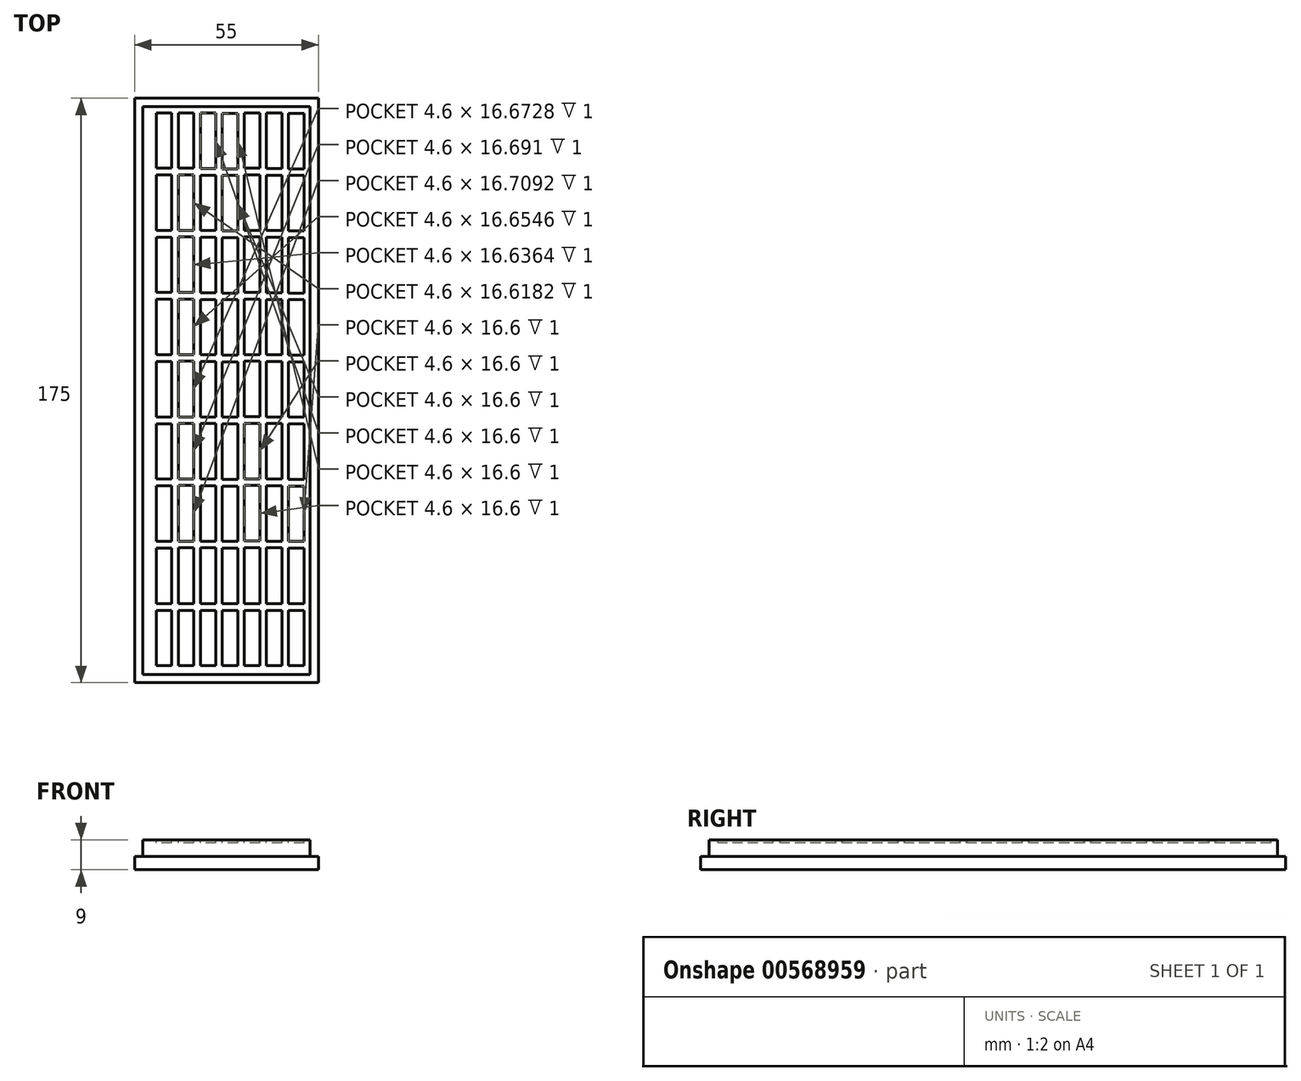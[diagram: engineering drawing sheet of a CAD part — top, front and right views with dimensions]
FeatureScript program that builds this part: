
annotation { "Feature Type Name" : "Feature", "Feature Type Description" : "" }
export const myFeature = defineFeature(function(context is Context, id is Id, definition is map)
    precondition{}
    {
        {
            var Q0;
            Q0=qCreatedBy(makeId("Top.planeOp"),FACE);
            var sketch = newSketch(context, id + "F0", { "sketchPlane" : qUnion([Q0])});
            skLineSegment(sketch, "E0.bottom", {"start": v(-26.96, 161.38) * mm, "end": v(28.04, 161.38) * mm});
            skLineSegment(sketch, "E0.top", {"start": v(-26.96, -13.62) * mm, "end": v(28.04, -13.62) * mm});
            skLineSegment(sketch, "E0.left", {"start": v(-26.96, 161.38) * mm, "end": v(-26.96, -13.62) * mm});
            skLineSegment(sketch, "E0.right", {"start": v(28.04, 161.38) * mm, "end": v(28.04, -13.62) * mm});
            skSolve(sketch);
        }
        {
            var Q0;
            Q0=makeQuery(id+"F0.imprint","IMPRINT",FACE,{"disambiguationData":[TD([[makeQuery(id+"F0.imprint","IMPRINT",EDGE,{"derivedFrom":sQuery(id+"F0.wireOp",EDGE,"E0.bottom")}),-1.0]])]});
            extrude(context, id + "F1", {"entities" : qUnion([Q0]), "depth" : 4 * mm, "offsetDistance" : 25.4 * mm});
        }
        {
            var Q0;
            Q0=makeQuery(id+"F1.opExtrude","CAP_FACE",FACE,{"disambiguationData":[OSD([sQuery(id+"F0.wireOp",EDGE,"E0.bottom"),sQuery(id+"F0.wireOp",EDGE,"E0.top"),sQuery(id+"F0.wireOp",EDGE,"E0.left"),sQuery(id+"F0.wireOp",EDGE,"E0.right")])],"isStart":false});
            var sketch = newSketch(context, id + "F2", { "sketchPlane" : qUnion([Q0])});
            skLineSegment(sketch, "E1.bottom", {"start": v(25.54, 158.88) * mm, "end": v(-24.46, 158.88) * mm});
            skLineSegment(sketch, "E1.top", {"start": v(25.54, -11.12) * mm, "end": v(-24.46, -11.12) * mm});
            skLineSegment(sketch, "E1.left", {"start": v(25.54, 158.88) * mm, "end": v(25.54, -11.12) * mm});
            skLineSegment(sketch, "E1.right", {"start": v(-24.46, 158.88) * mm, "end": v(-24.46, -11.12) * mm});
            skSolve(sketch);
        }
        {
            var Q0;
            Q0=makeQuery(id+"F2.imprint","IMPRINT",FACE,{"disambiguationData":[TD([[makeQuery(id+"F2.imprint","IMPRINT",EDGE,{"derivedFrom":sQuery(id+"F2.wireOp",EDGE,"E1.bottom")}),1.0]])]});
            extrude(context, id + "F3", {"entities" : qUnion([Q0]), "operationType" : NewBodyOperationType.ADD, "depth" : 5 * mm, "offsetDistance" : 25.4 * mm});
        }
        {
            var Q0;
            Q0=makeQuery(id+"F3.opExtrude","CAP_FACE",FACE,{"disambiguationData":[OSD([sQuery(id+"F2.wireOp",EDGE,"E1.bottom"),sQuery(id+"F2.wireOp",EDGE,"E1.top"),sQuery(id+"F2.wireOp",EDGE,"E1.left"),sQuery(id+"F2.wireOp",EDGE,"E1.right")])],"isStart":false});
            var sketch = newSketch(context, id + "F4", { "sketchPlane" : qUnion([Q0])});
            skLineSegment(sketch, "E2.bottom", {"start": v(23.73, 156.88) * mm, "end": v(19.13, 156.88) * mm});
            skLineSegment(sketch, "E2.top", {"start": v(23.73, 140.28) * mm, "end": v(19.13, 140.28) * mm});
            skLineSegment(sketch, "E2.left", {"start": v(23.73, 156.88) * mm, "end": v(23.73, 140.28) * mm});
            skLineSegment(sketch, "E2.right", {"start": v(19.13, 156.88) * mm, "end": v(19.13, 140.28) * mm});
            skLineSegment(sketch, "E3.bottom", {"start": v(23.73, 138.28) * mm, "end": v(19.13, 138.28) * mm});
            skLineSegment(sketch, "E3.top", {"start": v(23.73, 121.68) * mm, "end": v(19.13, 121.68) * mm});
            skLineSegment(sketch, "E3.left", {"start": v(23.73, 138.28) * mm, "end": v(23.73, 121.68) * mm});
            skLineSegment(sketch, "E3.right", {"start": v(19.13, 138.28) * mm, "end": v(19.13, 121.68) * mm});
            skLineSegment(sketch, "E4.1.0.0", {"start": v(17.13, 156.97) * mm, "end": v(12.53, 156.97) * mm});
            skLineSegment(sketch, "E4.1.0.1", {"start": v(17.13, 156.97) * mm, "end": v(17.13, 140.37) * mm});
            skLineSegment(sketch, "E4.1.0.2", {"start": v(12.53, 156.97) * mm, "end": v(12.53, 140.37) * mm});
            skLineSegment(sketch, "E4.1.0.3", {"start": v(17.13, 140.37) * mm, "end": v(12.53, 140.37) * mm});
            skLineSegment(sketch, "E4.1.0.4", {"start": v(17.13, 138.37) * mm, "end": v(12.53, 138.37) * mm});
            skLineSegment(sketch, "E4.1.0.5", {"start": v(17.13, 138.37) * mm, "end": v(17.13, 121.77) * mm});
            skLineSegment(sketch, "E4.1.0.6", {"start": v(12.53, 138.37) * mm, "end": v(12.53, 121.77) * mm});
            skLineSegment(sketch, "E4.1.0.7", {"start": v(17.13, 121.77) * mm, "end": v(12.53, 121.77) * mm});
            skLineSegment(sketch, "E4.2.0.0", {"start": v(10.53, 157.05) * mm, "end": v(5.93, 157.05) * mm});
            skLineSegment(sketch, "E4.2.0.1", {"start": v(10.53, 157.05) * mm, "end": v(10.53, 140.45) * mm});
            skLineSegment(sketch, "E4.2.0.2", {"start": v(5.93, 157.05) * mm, "end": v(5.93, 140.45) * mm});
            skLineSegment(sketch, "E4.2.0.3", {"start": v(10.53, 140.45) * mm, "end": v(5.93, 140.45) * mm});
            skLineSegment(sketch, "E4.2.0.4", {"start": v(10.53, 138.45) * mm, "end": v(5.93, 138.45) * mm});
            skLineSegment(sketch, "E4.2.0.5", {"start": v(10.53, 138.45) * mm, "end": v(10.53, 121.85) * mm});
            skLineSegment(sketch, "E4.2.0.6", {"start": v(5.93, 138.45) * mm, "end": v(5.93, 121.85) * mm});
            skLineSegment(sketch, "E4.2.0.7", {"start": v(10.53, 121.85) * mm, "end": v(5.93, 121.85) * mm});
            skLineSegment(sketch, "E5.0.1.0", {"start": v(23.73, 119.68) * mm, "end": v(19.13, 119.68) * mm});
            skLineSegment(sketch, "E5.0.1.1", {"start": v(23.73, 119.68) * mm, "end": v(23.73, 103.08) * mm});
            skLineSegment(sketch, "E5.0.1.2", {"start": v(19.13, 119.68) * mm, "end": v(19.13, 103.08) * mm});
            skLineSegment(sketch, "E5.0.1.3", {"start": v(17.13, 119.77) * mm, "end": v(17.13, 103.17) * mm});
            skLineSegment(sketch, "E5.0.1.4", {"start": v(23.73, 103.08) * mm, "end": v(19.13, 103.08) * mm});
            skLineSegment(sketch, "E5.0.1.5", {"start": v(23.73, 101.08) * mm, "end": v(19.13, 101.08) * mm});
            skLineSegment(sketch, "E5.0.1.6", {"start": v(23.73, 101.08) * mm, "end": v(23.73, 84.48) * mm});
            skLineSegment(sketch, "E5.0.1.7", {"start": v(23.73, 84.48) * mm, "end": v(19.13, 84.48) * mm});
            skLineSegment(sketch, "E5.0.1.8", {"start": v(17.13, 101.17) * mm, "end": v(17.13, 84.57) * mm});
            skLineSegment(sketch, "E5.0.1.9", {"start": v(19.13, 101.08) * mm, "end": v(19.13, 84.48) * mm});
            skLineSegment(sketch, "E5.0.1.10", {"start": v(17.13, 101.17) * mm, "end": v(12.53, 101.17) * mm});
            skLineSegment(sketch, "E5.0.1.11", {"start": v(17.13, 103.17) * mm, "end": v(12.53, 103.17) * mm});
            skLineSegment(sketch, "E5.0.1.12", {"start": v(17.13, 119.77) * mm, "end": v(12.53, 119.77) * mm});
            skLineSegment(sketch, "E5.0.1.13", {"start": v(17.13, 84.57) * mm, "end": v(12.53, 84.57) * mm});
            skLineSegment(sketch, "E5.0.1.14", {"start": v(12.53, 101.17) * mm, "end": v(12.53, 84.57) * mm});
            skLineSegment(sketch, "E5.0.1.15", {"start": v(12.53, 119.77) * mm, "end": v(12.53, 103.17) * mm});
            skLineSegment(sketch, "E5.0.1.16", {"start": v(10.53, 119.85) * mm, "end": v(10.53, 103.25) * mm});
            skLineSegment(sketch, "E5.0.1.17", {"start": v(10.53, 119.85) * mm, "end": v(5.93, 119.85) * mm});
            skLineSegment(sketch, "E5.0.1.18", {"start": v(5.93, 119.85) * mm, "end": v(5.93, 103.25) * mm});
            skLineSegment(sketch, "E5.0.1.19", {"start": v(10.53, 103.25) * mm, "end": v(5.93, 103.25) * mm});
            skLineSegment(sketch, "E5.0.1.20", {"start": v(10.53, 101.25) * mm, "end": v(5.93, 101.25) * mm});
            skLineSegment(sketch, "E5.0.1.21", {"start": v(10.53, 101.25) * mm, "end": v(10.53, 84.65) * mm});
            skLineSegment(sketch, "E5.0.1.22", {"start": v(5.93, 101.25) * mm, "end": v(5.93, 84.65) * mm});
            skLineSegment(sketch, "E5.0.1.23", {"start": v(10.53, 84.65) * mm, "end": v(5.93, 84.65) * mm});
            skLineSegment(sketch, "E5.0.2.0", {"start": v(23.73, 82.48) * mm, "end": v(19.13, 82.48) * mm});
            skLineSegment(sketch, "E5.0.2.1", {"start": v(23.73, 82.48) * mm, "end": v(23.73, 65.88) * mm});
            skLineSegment(sketch, "E5.0.2.2", {"start": v(19.13, 82.48) * mm, "end": v(19.13, 65.88) * mm});
            skLineSegment(sketch, "E5.0.2.3", {"start": v(17.13, 82.57) * mm, "end": v(17.13, 65.97) * mm});
            skLineSegment(sketch, "E5.0.2.4", {"start": v(23.73, 65.88) * mm, "end": v(19.13, 65.88) * mm});
            skLineSegment(sketch, "E5.0.2.5", {"start": v(23.73, 63.88) * mm, "end": v(19.13, 63.88) * mm});
            skLineSegment(sketch, "E5.0.2.6", {"start": v(23.73, 63.88) * mm, "end": v(23.73, 47.28) * mm});
            skLineSegment(sketch, "E5.0.2.7", {"start": v(23.73, 47.28) * mm, "end": v(19.13, 47.28) * mm});
            skLineSegment(sketch, "E5.0.2.8", {"start": v(17.13, 63.97) * mm, "end": v(17.13, 47.37) * mm});
            skLineSegment(sketch, "E5.0.2.9", {"start": v(19.13, 63.88) * mm, "end": v(19.13, 47.28) * mm});
            skLineSegment(sketch, "E5.0.2.10", {"start": v(17.13, 63.97) * mm, "end": v(12.53, 63.97) * mm});
            skLineSegment(sketch, "E5.0.2.11", {"start": v(17.13, 65.97) * mm, "end": v(12.53, 65.97) * mm});
            skLineSegment(sketch, "E5.0.2.12", {"start": v(17.13, 82.57) * mm, "end": v(12.53, 82.57) * mm});
            skLineSegment(sketch, "E5.0.2.13", {"start": v(17.13, 47.37) * mm, "end": v(12.53, 47.37) * mm});
            skLineSegment(sketch, "E5.0.2.14", {"start": v(12.53, 63.97) * mm, "end": v(12.53, 47.37) * mm});
            skLineSegment(sketch, "E5.0.2.15", {"start": v(12.53, 82.57) * mm, "end": v(12.53, 65.97) * mm});
            skLineSegment(sketch, "E5.0.2.16", {"start": v(10.53, 82.65) * mm, "end": v(10.53, 66.05) * mm});
            skLineSegment(sketch, "E5.0.2.17", {"start": v(10.53, 82.65) * mm, "end": v(5.93, 82.65) * mm});
            skLineSegment(sketch, "E5.0.2.18", {"start": v(5.93, 82.65) * mm, "end": v(5.93, 66.05) * mm});
            skLineSegment(sketch, "E5.0.2.19", {"start": v(10.53, 66.05) * mm, "end": v(5.93, 66.05) * mm});
            skLineSegment(sketch, "E5.0.2.20", {"start": v(10.53, 64.05) * mm, "end": v(5.93, 64.05) * mm});
            skLineSegment(sketch, "E5.0.2.21", {"start": v(10.53, 64.05) * mm, "end": v(10.53, 47.45) * mm});
            skLineSegment(sketch, "E5.0.2.22", {"start": v(5.93, 64.05) * mm, "end": v(5.93, 47.45) * mm});
            skLineSegment(sketch, "E5.0.2.23", {"start": v(10.53, 47.45) * mm, "end": v(5.93, 47.45) * mm});
            skLineSegment(sketch, "E5.0.3.0", {"start": v(23.73, 45.28) * mm, "end": v(19.13, 45.28) * mm});
            skLineSegment(sketch, "E5.0.3.1", {"start": v(23.73, 45.28) * mm, "end": v(23.73, 28.68) * mm});
            skLineSegment(sketch, "E5.0.3.2", {"start": v(19.13, 45.28) * mm, "end": v(19.13, 28.68) * mm});
            skLineSegment(sketch, "E5.0.3.3", {"start": v(17.13, 45.37) * mm, "end": v(17.13, 28.77) * mm});
            skLineSegment(sketch, "E5.0.3.4", {"start": v(23.73, 28.68) * mm, "end": v(19.13, 28.68) * mm});
            skLineSegment(sketch, "E5.0.3.5", {"start": v(23.73, 26.68) * mm, "end": v(19.13, 26.68) * mm});
            skLineSegment(sketch, "E5.0.3.6", {"start": v(23.73, 26.68) * mm, "end": v(23.73, 10.08) * mm});
            skLineSegment(sketch, "E5.0.3.7", {"start": v(23.73, 10.08) * mm, "end": v(19.13, 10.08) * mm});
            skLineSegment(sketch, "E5.0.3.8", {"start": v(17.13, 26.77) * mm, "end": v(17.13, 10.17) * mm});
            skLineSegment(sketch, "E5.0.3.9", {"start": v(19.13, 26.68) * mm, "end": v(19.13, 10.08) * mm});
            skLineSegment(sketch, "E5.0.3.10", {"start": v(17.13, 26.77) * mm, "end": v(12.53, 26.77) * mm});
            skLineSegment(sketch, "E5.0.3.11", {"start": v(17.13, 28.77) * mm, "end": v(12.53, 28.77) * mm});
            skLineSegment(sketch, "E5.0.3.12", {"start": v(17.13, 45.37) * mm, "end": v(12.53, 45.37) * mm});
            skLineSegment(sketch, "E5.0.3.13", {"start": v(17.13, 10.17) * mm, "end": v(12.53, 10.17) * mm});
            skLineSegment(sketch, "E5.0.3.14", {"start": v(12.53, 26.77) * mm, "end": v(12.53, 10.17) * mm});
            skLineSegment(sketch, "E5.0.3.15", {"start": v(12.53, 45.37) * mm, "end": v(12.53, 28.77) * mm});
            skLineSegment(sketch, "E5.0.3.16", {"start": v(10.53, 45.45) * mm, "end": v(10.53, 28.85) * mm});
            skLineSegment(sketch, "E5.0.3.17", {"start": v(10.53, 45.45) * mm, "end": v(5.93, 45.45) * mm});
            skLineSegment(sketch, "E5.0.3.18", {"start": v(5.93, 45.45) * mm, "end": v(5.93, 28.85) * mm});
            skLineSegment(sketch, "E5.0.3.19", {"start": v(10.53, 28.85) * mm, "end": v(5.93, 28.85) * mm});
            skLineSegment(sketch, "E5.0.3.20", {"start": v(10.53, 26.85) * mm, "end": v(5.93, 26.85) * mm});
            skLineSegment(sketch, "E5.0.3.21", {"start": v(10.53, 26.85) * mm, "end": v(10.53, 10.25) * mm});
            skLineSegment(sketch, "E5.0.3.22", {"start": v(5.93, 26.85) * mm, "end": v(5.93, 10.25) * mm});
            skLineSegment(sketch, "E5.0.3.23", {"start": v(10.53, 10.25) * mm, "end": v(5.93, 10.25) * mm});
            skLineSegment(sketch, "E5.1.0.0", {"start": v(3.93, 156.88) * mm, "end": v(-0.67, 156.88) * mm});
            skLineSegment(sketch, "E5.1.0.1", {"start": v(3.93, 156.88) * mm, "end": v(3.93, 140.28) * mm});
            skLineSegment(sketch, "E5.1.0.2", {"start": v(-0.67, 156.88) * mm, "end": v(-0.67, 140.28) * mm});
            skLineSegment(sketch, "E5.1.0.3", {"start": v(-2.67, 156.97) * mm, "end": v(-2.67, 140.37) * mm});
            skLineSegment(sketch, "E5.1.0.4", {"start": v(3.93, 140.28) * mm, "end": v(-0.67, 140.28) * mm});
            skLineSegment(sketch, "E5.1.0.5", {"start": v(3.93, 138.28) * mm, "end": v(-0.67, 138.28) * mm});
            skLineSegment(sketch, "E5.1.0.6", {"start": v(3.93, 138.28) * mm, "end": v(3.93, 121.68) * mm});
            skLineSegment(sketch, "E5.1.0.7", {"start": v(3.93, 121.68) * mm, "end": v(-0.67, 121.68) * mm});
            skLineSegment(sketch, "E5.1.0.8", {"start": v(-2.67, 138.37) * mm, "end": v(-2.67, 121.77) * mm});
            skLineSegment(sketch, "E5.1.0.9", {"start": v(-0.67, 138.28) * mm, "end": v(-0.67, 121.68) * mm});
            skLineSegment(sketch, "E5.1.0.10", {"start": v(-2.67, 138.37) * mm, "end": v(-7.27, 138.37) * mm});
            skLineSegment(sketch, "E5.1.0.11", {"start": v(-2.67, 140.37) * mm, "end": v(-7.27, 140.37) * mm});
            skLineSegment(sketch, "E5.1.0.12", {"start": v(-2.67, 156.97) * mm, "end": v(-7.27, 156.97) * mm});
            skLineSegment(sketch, "E5.1.0.13", {"start": v(-2.67, 121.77) * mm, "end": v(-7.27, 121.77) * mm});
            skLineSegment(sketch, "E5.1.0.14", {"start": v(-7.27, 138.37) * mm, "end": v(-7.27, 121.77) * mm});
            skLineSegment(sketch, "E5.1.0.15", {"start": v(-7.27, 156.97) * mm, "end": v(-7.27, 140.37) * mm});
            skLineSegment(sketch, "E5.1.0.16", {"start": v(-9.27, 157.05) * mm, "end": v(-9.27, 140.45) * mm});
            skLineSegment(sketch, "E5.1.0.17", {"start": v(-9.27, 157.05) * mm, "end": v(-13.87, 157.05) * mm});
            skLineSegment(sketch, "E5.1.0.18", {"start": v(-13.87, 157.05) * mm, "end": v(-13.87, 140.45) * mm});
            skLineSegment(sketch, "E5.1.0.19", {"start": v(-9.27, 140.45) * mm, "end": v(-13.87, 140.45) * mm});
            skLineSegment(sketch, "E5.1.0.20", {"start": v(-9.27, 138.45) * mm, "end": v(-13.87, 138.45) * mm});
            skLineSegment(sketch, "E5.1.0.21", {"start": v(-9.27, 138.45) * mm, "end": v(-9.27, 121.85) * mm});
            skLineSegment(sketch, "E5.1.0.22", {"start": v(-13.87, 138.45) * mm, "end": v(-13.87, 121.85) * mm});
            skLineSegment(sketch, "E5.1.0.23", {"start": v(-9.27, 121.85) * mm, "end": v(-13.87, 121.85) * mm});
            skLineSegment(sketch, "E5.1.1.0", {"start": v(3.93, 119.68) * mm, "end": v(-0.67, 119.68) * mm});
            skLineSegment(sketch, "E5.1.1.1", {"start": v(3.93, 119.68) * mm, "end": v(3.93, 103.08) * mm});
            skLineSegment(sketch, "E5.1.1.2", {"start": v(-0.67, 119.68) * mm, "end": v(-0.67, 103.08) * mm});
            skLineSegment(sketch, "E5.1.1.3", {"start": v(-2.67, 119.77) * mm, "end": v(-2.67, 103.17) * mm});
            skLineSegment(sketch, "E5.1.1.4", {"start": v(3.93, 103.08) * mm, "end": v(-0.67, 103.08) * mm});
            skLineSegment(sketch, "E5.1.1.5", {"start": v(3.93, 101.08) * mm, "end": v(-0.67, 101.08) * mm});
            skLineSegment(sketch, "E5.1.1.6", {"start": v(3.93, 101.08) * mm, "end": v(3.93, 84.48) * mm});
            skLineSegment(sketch, "E5.1.1.7", {"start": v(3.93, 84.48) * mm, "end": v(-0.67, 84.48) * mm});
            skLineSegment(sketch, "E5.1.1.8", {"start": v(-2.67, 101.17) * mm, "end": v(-2.67, 84.57) * mm});
            skLineSegment(sketch, "E5.1.1.9", {"start": v(-0.67, 101.08) * mm, "end": v(-0.67, 84.48) * mm});
            skLineSegment(sketch, "E5.1.1.10", {"start": v(-2.67, 101.17) * mm, "end": v(-7.27, 101.17) * mm});
            skLineSegment(sketch, "E5.1.1.11", {"start": v(-2.67, 103.17) * mm, "end": v(-7.27, 103.17) * mm});
            skLineSegment(sketch, "E5.1.1.12", {"start": v(-2.67, 119.77) * mm, "end": v(-7.27, 119.77) * mm});
            skLineSegment(sketch, "E5.1.1.13", {"start": v(-2.67, 84.57) * mm, "end": v(-7.27, 84.57) * mm});
            skLineSegment(sketch, "E5.1.1.14", {"start": v(-7.27, 101.17) * mm, "end": v(-7.27, 84.57) * mm});
            skLineSegment(sketch, "E5.1.1.15", {"start": v(-7.27, 119.77) * mm, "end": v(-7.27, 103.17) * mm});
            skLineSegment(sketch, "E5.1.1.16", {"start": v(-9.27, 119.85) * mm, "end": v(-9.27, 103.25) * mm});
            skLineSegment(sketch, "E5.1.1.17", {"start": v(-9.27, 119.85) * mm, "end": v(-13.87, 119.85) * mm});
            skLineSegment(sketch, "E5.1.1.18", {"start": v(-13.87, 119.85) * mm, "end": v(-13.87, 103.25) * mm});
            skLineSegment(sketch, "E5.1.1.19", {"start": v(-9.27, 103.25) * mm, "end": v(-13.87, 103.25) * mm});
            skLineSegment(sketch, "E5.1.1.20", {"start": v(-9.27, 101.25) * mm, "end": v(-13.87, 101.25) * mm});
            skLineSegment(sketch, "E5.1.1.21", {"start": v(-9.27, 101.25) * mm, "end": v(-9.27, 84.65) * mm});
            skLineSegment(sketch, "E5.1.1.22", {"start": v(-13.87, 101.25) * mm, "end": v(-13.87, 84.65) * mm});
            skLineSegment(sketch, "E5.1.1.23", {"start": v(-9.27, 84.65) * mm, "end": v(-13.87, 84.65) * mm});
            skLineSegment(sketch, "E5.1.2.0", {"start": v(3.93, 82.48) * mm, "end": v(-0.67, 82.48) * mm});
            skLineSegment(sketch, "E5.1.2.1", {"start": v(3.93, 82.48) * mm, "end": v(3.93, 65.88) * mm});
            skLineSegment(sketch, "E5.1.2.2", {"start": v(-0.67, 82.48) * mm, "end": v(-0.67, 65.88) * mm});
            skLineSegment(sketch, "E5.1.2.3", {"start": v(-2.67, 82.57) * mm, "end": v(-2.67, 65.97) * mm});
            skLineSegment(sketch, "E5.1.2.4", {"start": v(3.93, 65.88) * mm, "end": v(-0.67, 65.88) * mm});
            skLineSegment(sketch, "E5.1.2.5", {"start": v(3.93, 63.88) * mm, "end": v(-0.67, 63.88) * mm});
            skLineSegment(sketch, "E5.1.2.6", {"start": v(3.93, 63.88) * mm, "end": v(3.93, 47.28) * mm});
            skLineSegment(sketch, "E5.1.2.7", {"start": v(3.93, 47.28) * mm, "end": v(-0.67, 47.28) * mm});
            skLineSegment(sketch, "E5.1.2.8", {"start": v(-2.67, 63.97) * mm, "end": v(-2.67, 47.37) * mm});
            skLineSegment(sketch, "E5.1.2.9", {"start": v(-0.67, 63.88) * mm, "end": v(-0.67, 47.28) * mm});
            skLineSegment(sketch, "E5.1.2.10", {"start": v(-2.67, 63.97) * mm, "end": v(-7.27, 63.97) * mm});
            skLineSegment(sketch, "E5.1.2.11", {"start": v(-2.67, 65.97) * mm, "end": v(-7.27, 65.97) * mm});
            skLineSegment(sketch, "E5.1.2.12", {"start": v(-2.67, 82.57) * mm, "end": v(-7.27, 82.57) * mm});
            skLineSegment(sketch, "E5.1.2.13", {"start": v(-2.67, 47.37) * mm, "end": v(-7.27, 47.37) * mm});
            skLineSegment(sketch, "E5.1.2.14", {"start": v(-7.27, 63.97) * mm, "end": v(-7.27, 47.37) * mm});
            skLineSegment(sketch, "E5.1.2.15", {"start": v(-7.27, 82.57) * mm, "end": v(-7.27, 65.97) * mm});
            skLineSegment(sketch, "E5.1.2.16", {"start": v(-9.27, 82.65) * mm, "end": v(-9.27, 66.05) * mm});
            skLineSegment(sketch, "E5.1.2.17", {"start": v(-9.27, 82.65) * mm, "end": v(-13.87, 82.65) * mm});
            skLineSegment(sketch, "E5.1.2.18", {"start": v(-13.87, 82.65) * mm, "end": v(-13.87, 66.05) * mm});
            skLineSegment(sketch, "E5.1.2.19", {"start": v(-9.27, 66.05) * mm, "end": v(-13.87, 66.05) * mm});
            skLineSegment(sketch, "E5.1.2.20", {"start": v(-9.27, 64.05) * mm, "end": v(-13.87, 64.05) * mm});
            skLineSegment(sketch, "E5.1.2.21", {"start": v(-9.27, 64.05) * mm, "end": v(-9.27, 47.45) * mm});
            skLineSegment(sketch, "E5.1.2.22", {"start": v(-13.87, 64.05) * mm, "end": v(-13.87, 47.45) * mm});
            skLineSegment(sketch, "E5.1.2.23", {"start": v(-9.27, 47.45) * mm, "end": v(-13.87, 47.45) * mm});
            skLineSegment(sketch, "E5.1.3.0", {"start": v(3.93, 45.28) * mm, "end": v(-0.67, 45.28) * mm});
            skLineSegment(sketch, "E5.1.3.1", {"start": v(3.93, 45.28) * mm, "end": v(3.93, 28.68) * mm});
            skLineSegment(sketch, "E5.1.3.2", {"start": v(-0.67, 45.28) * mm, "end": v(-0.67, 28.68) * mm});
            skLineSegment(sketch, "E5.1.3.3", {"start": v(-2.67, 45.37) * mm, "end": v(-2.67, 28.77) * mm});
            skLineSegment(sketch, "E5.1.3.4", {"start": v(3.93, 28.68) * mm, "end": v(-0.67, 28.68) * mm});
            skLineSegment(sketch, "E5.1.3.5", {"start": v(3.93, 26.68) * mm, "end": v(-0.67, 26.68) * mm});
            skLineSegment(sketch, "E5.1.3.6", {"start": v(3.93, 26.68) * mm, "end": v(3.93, 10.08) * mm});
            skLineSegment(sketch, "E5.1.3.7", {"start": v(3.93, 10.08) * mm, "end": v(-0.67, 10.08) * mm});
            skLineSegment(sketch, "E5.1.3.8", {"start": v(-2.67, 26.77) * mm, "end": v(-2.67, 10.17) * mm});
            skLineSegment(sketch, "E5.1.3.9", {"start": v(-0.67, 26.68) * mm, "end": v(-0.67, 10.08) * mm});
            skLineSegment(sketch, "E5.1.3.10", {"start": v(-2.67, 26.77) * mm, "end": v(-7.27, 26.77) * mm});
            skLineSegment(sketch, "E5.1.3.11", {"start": v(-2.67, 28.77) * mm, "end": v(-7.27, 28.77) * mm});
            skLineSegment(sketch, "E5.1.3.12", {"start": v(-2.67, 45.37) * mm, "end": v(-7.27, 45.37) * mm});
            skLineSegment(sketch, "E5.1.3.13", {"start": v(-2.67, 10.17) * mm, "end": v(-7.27, 10.17) * mm});
            skLineSegment(sketch, "E5.1.3.14", {"start": v(-7.27, 26.77) * mm, "end": v(-7.27, 10.17) * mm});
            skLineSegment(sketch, "E5.1.3.15", {"start": v(-7.27, 45.37) * mm, "end": v(-7.27, 28.77) * mm});
            skLineSegment(sketch, "E5.1.3.16", {"start": v(-9.27, 45.45) * mm, "end": v(-9.27, 28.85) * mm});
            skLineSegment(sketch, "E5.1.3.17", {"start": v(-9.27, 45.45) * mm, "end": v(-13.87, 45.45) * mm});
            skLineSegment(sketch, "E5.1.3.18", {"start": v(-13.87, 45.45) * mm, "end": v(-13.87, 28.85) * mm});
            skLineSegment(sketch, "E5.1.3.19", {"start": v(-9.27, 28.85) * mm, "end": v(-13.87, 28.85) * mm});
            skLineSegment(sketch, "E5.1.3.20", {"start": v(-9.27, 26.85) * mm, "end": v(-13.87, 26.85) * mm});
            skLineSegment(sketch, "E5.1.3.21", {"start": v(-9.27, 26.85) * mm, "end": v(-9.27, 10.25) * mm});
            skLineSegment(sketch, "E5.1.3.22", {"start": v(-13.87, 26.85) * mm, "end": v(-13.87, 10.25) * mm});
            skLineSegment(sketch, "E5.1.3.23", {"start": v(-9.27, 10.25) * mm, "end": v(-13.87, 10.25) * mm});
            skLineSegment(sketch, "E6.0.1.0", {"start": v(-13.87, 138.44) * mm, "end": v(-13.87, 121.84) * mm});
            skLineSegment(sketch, "E6.0.1.1", {"start": v(-9.27, 138.44) * mm, "end": v(-13.87, 138.44) * mm});
            skLineSegment(sketch, "E6.0.1.2", {"start": v(-9.27, 138.44) * mm, "end": v(-9.27, 121.84) * mm});
            skLineSegment(sketch, "E6.0.1.3", {"start": v(-9.27, 121.84) * mm, "end": v(-13.87, 121.84) * mm});
            skLineSegment(sketch, "E6.0.2.0", {"start": v(-13.87, 119.82) * mm, "end": v(-13.87, 103.22) * mm});
            skLineSegment(sketch, "E6.0.2.1", {"start": v(-9.27, 119.82) * mm, "end": v(-13.87, 119.82) * mm});
            skLineSegment(sketch, "E6.0.2.2", {"start": v(-9.27, 119.82) * mm, "end": v(-9.27, 103.22) * mm});
            skLineSegment(sketch, "E6.0.2.3", {"start": v(-9.27, 103.22) * mm, "end": v(-13.87, 103.22) * mm});
            skLineSegment(sketch, "E6.0.3.0", {"start": v(-13.87, 101.2) * mm, "end": v(-13.87, 84.6) * mm});
            skLineSegment(sketch, "E6.0.3.1", {"start": v(-9.27, 101.2) * mm, "end": v(-13.87, 101.2) * mm});
            skLineSegment(sketch, "E6.0.3.2", {"start": v(-9.27, 101.2) * mm, "end": v(-9.27, 84.6) * mm});
            skLineSegment(sketch, "E6.0.3.3", {"start": v(-9.27, 84.6) * mm, "end": v(-13.87, 84.6) * mm});
            skLineSegment(sketch, "E6.0.4.0", {"start": v(-13.87, 82.58) * mm, "end": v(-13.87, 65.98) * mm});
            skLineSegment(sketch, "E6.0.4.1", {"start": v(-9.27, 82.58) * mm, "end": v(-13.87, 82.58) * mm});
            skLineSegment(sketch, "E6.0.4.2", {"start": v(-9.27, 82.58) * mm, "end": v(-9.27, 65.98) * mm});
            skLineSegment(sketch, "E6.0.4.3", {"start": v(-9.27, 65.98) * mm, "end": v(-13.87, 65.98) * mm});
            skLineSegment(sketch, "E6.0.5.0", {"start": v(-13.87, 63.96) * mm, "end": v(-13.87, 47.36) * mm});
            skLineSegment(sketch, "E6.0.5.1", {"start": v(-9.27, 63.96) * mm, "end": v(-13.87, 63.96) * mm});
            skLineSegment(sketch, "E6.0.5.2", {"start": v(-9.27, 63.96) * mm, "end": v(-9.27, 47.36) * mm});
            skLineSegment(sketch, "E6.0.5.3", {"start": v(-9.27, 47.36) * mm, "end": v(-13.87, 47.36) * mm});
            skLineSegment(sketch, "E6.0.6.0", {"start": v(-13.87, 45.35) * mm, "end": v(-13.87, 28.75) * mm});
            skLineSegment(sketch, "E6.0.6.1", {"start": v(-9.27, 45.35) * mm, "end": v(-13.87, 45.35) * mm});
            skLineSegment(sketch, "E6.0.6.2", {"start": v(-9.27, 45.35) * mm, "end": v(-9.27, 28.75) * mm});
            skLineSegment(sketch, "E6.0.6.3", {"start": v(-9.27, 28.75) * mm, "end": v(-13.87, 28.75) * mm});
            skLineSegment(sketch, "E6.0.7.0", {"start": v(-13.87, 26.73) * mm, "end": v(-13.87, 10.13) * mm});
            skLineSegment(sketch, "E6.0.7.1", {"start": v(-9.27, 26.73) * mm, "end": v(-13.87, 26.73) * mm});
            skLineSegment(sketch, "E6.0.7.2", {"start": v(-9.27, 26.73) * mm, "end": v(-9.27, 10.13) * mm});
            skLineSegment(sketch, "E6.0.7.3", {"start": v(-9.27, 10.13) * mm, "end": v(-13.87, 10.13) * mm});
            skLineSegment(sketch, "E6.1.0.0", {"start": v(-20.47, 157.05) * mm, "end": v(-20.47, 140.45) * mm});
            skLineSegment(sketch, "E6.1.0.1", {"start": v(-15.87, 157.05) * mm, "end": v(-20.47, 157.05) * mm});
            skLineSegment(sketch, "E6.1.0.2", {"start": v(-15.87, 157.05) * mm, "end": v(-15.87, 140.45) * mm});
            skLineSegment(sketch, "E6.1.0.3", {"start": v(-15.87, 140.45) * mm, "end": v(-20.47, 140.45) * mm});
            skLineSegment(sketch, "E6.1.1.0", {"start": v(-20.47, 138.44) * mm, "end": v(-20.47, 121.84) * mm});
            skLineSegment(sketch, "E6.1.1.1", {"start": v(-15.87, 138.44) * mm, "end": v(-20.47, 138.44) * mm});
            skLineSegment(sketch, "E6.1.1.2", {"start": v(-15.87, 138.44) * mm, "end": v(-15.87, 121.84) * mm});
            skLineSegment(sketch, "E6.1.1.3", {"start": v(-15.87, 121.84) * mm, "end": v(-20.47, 121.84) * mm});
            skLineSegment(sketch, "E6.1.2.0", {"start": v(-20.47, 119.82) * mm, "end": v(-20.47, 103.22) * mm});
            skLineSegment(sketch, "E6.1.2.1", {"start": v(-15.87, 119.82) * mm, "end": v(-20.47, 119.82) * mm});
            skLineSegment(sketch, "E6.1.2.2", {"start": v(-15.87, 119.82) * mm, "end": v(-15.87, 103.22) * mm});
            skLineSegment(sketch, "E6.1.2.3", {"start": v(-15.87, 103.22) * mm, "end": v(-20.47, 103.22) * mm});
            skLineSegment(sketch, "E6.1.3.0", {"start": v(-20.47, 101.2) * mm, "end": v(-20.47, 84.6) * mm});
            skLineSegment(sketch, "E6.1.3.1", {"start": v(-15.87, 101.2) * mm, "end": v(-20.47, 101.2) * mm});
            skLineSegment(sketch, "E6.1.3.2", {"start": v(-15.87, 101.2) * mm, "end": v(-15.87, 84.6) * mm});
            skLineSegment(sketch, "E6.1.3.3", {"start": v(-15.87, 84.6) * mm, "end": v(-20.47, 84.6) * mm});
            skLineSegment(sketch, "E6.1.4.0", {"start": v(-20.47, 82.58) * mm, "end": v(-20.47, 65.98) * mm});
            skLineSegment(sketch, "E6.1.4.1", {"start": v(-15.87, 82.58) * mm, "end": v(-20.47, 82.58) * mm});
            skLineSegment(sketch, "E6.1.4.2", {"start": v(-15.87, 82.58) * mm, "end": v(-15.87, 65.98) * mm});
            skLineSegment(sketch, "E6.1.4.3", {"start": v(-15.87, 65.98) * mm, "end": v(-20.47, 65.98) * mm});
            skLineSegment(sketch, "E6.1.5.0", {"start": v(-20.47, 63.96) * mm, "end": v(-20.47, 47.36) * mm});
            skLineSegment(sketch, "E6.1.5.1", {"start": v(-15.87, 63.96) * mm, "end": v(-20.47, 63.96) * mm});
            skLineSegment(sketch, "E6.1.5.2", {"start": v(-15.87, 63.96) * mm, "end": v(-15.87, 47.36) * mm});
            skLineSegment(sketch, "E6.1.5.3", {"start": v(-15.87, 47.36) * mm, "end": v(-20.47, 47.36) * mm});
            skLineSegment(sketch, "E6.1.6.0", {"start": v(-20.47, 45.35) * mm, "end": v(-20.47, 28.75) * mm});
            skLineSegment(sketch, "E6.1.6.1", {"start": v(-15.87, 45.35) * mm, "end": v(-20.47, 45.35) * mm});
            skLineSegment(sketch, "E6.1.6.2", {"start": v(-15.87, 45.35) * mm, "end": v(-15.87, 28.75) * mm});
            skLineSegment(sketch, "E6.1.6.3", {"start": v(-15.87, 28.75) * mm, "end": v(-20.47, 28.75) * mm});
            skLineSegment(sketch, "E6.1.7.0", {"start": v(-20.47, 26.73) * mm, "end": v(-20.47, 10.13) * mm});
            skLineSegment(sketch, "E6.1.7.1", {"start": v(-15.87, 26.73) * mm, "end": v(-20.47, 26.73) * mm});
            skLineSegment(sketch, "E6.1.7.2", {"start": v(-15.87, 26.73) * mm, "end": v(-15.87, 10.13) * mm});
            skLineSegment(sketch, "E6.1.7.3", {"start": v(-15.87, 10.13) * mm, "end": v(-20.47, 10.13) * mm});
            skLineSegment(sketch, "E7.0.1.0", {"start": v(23.73, 8.08) * mm, "end": v(23.73, -8.52) * mm});
            skLineSegment(sketch, "E7.0.1.1", {"start": v(19.13, 8.08) * mm, "end": v(19.13, -8.52) * mm});
            skLineSegment(sketch, "E7.0.1.2", {"start": v(23.73, 8.08) * mm, "end": v(19.13, 8.08) * mm});
            skLineSegment(sketch, "E7.0.1.3", {"start": v(23.73, -8.52) * mm, "end": v(19.13, -8.52) * mm});
            skLineSegment(sketch, "E7.1.0.0", {"start": v(17.13, 26.68) * mm, "end": v(17.13, 10.08) * mm});
            skLineSegment(sketch, "E7.1.0.1", {"start": v(12.53, 26.68) * mm, "end": v(12.53, 10.08) * mm});
            skLineSegment(sketch, "E7.1.0.2", {"start": v(17.13, 26.68) * mm, "end": v(12.53, 26.68) * mm});
            skLineSegment(sketch, "E7.1.0.3", {"start": v(17.13, 10.08) * mm, "end": v(12.53, 10.08) * mm});
            skLineSegment(sketch, "E7.1.1.0", {"start": v(17.13, 8.08) * mm, "end": v(17.13, -8.52) * mm});
            skLineSegment(sketch, "E7.1.1.1", {"start": v(12.53, 8.08) * mm, "end": v(12.53, -8.52) * mm});
            skLineSegment(sketch, "E7.1.1.2", {"start": v(17.13, 8.08) * mm, "end": v(12.53, 8.08) * mm});
            skLineSegment(sketch, "E7.1.1.3", {"start": v(17.13, -8.52) * mm, "end": v(12.53, -8.52) * mm});
            skLineSegment(sketch, "E7.2.0.0", {"start": v(10.53, 26.68) * mm, "end": v(10.53, 10.08) * mm});
            skLineSegment(sketch, "E7.2.0.1", {"start": v(5.93, 26.68) * mm, "end": v(5.93, 10.08) * mm});
            skLineSegment(sketch, "E7.2.0.2", {"start": v(10.53, 26.68) * mm, "end": v(5.93, 26.68) * mm});
            skLineSegment(sketch, "E7.2.0.3", {"start": v(10.53, 10.08) * mm, "end": v(5.93, 10.08) * mm});
            skLineSegment(sketch, "E7.2.1.0", {"start": v(10.53, 8.08) * mm, "end": v(10.53, -8.52) * mm});
            skLineSegment(sketch, "E7.2.1.1", {"start": v(5.93, 8.08) * mm, "end": v(5.93, -8.52) * mm});
            skLineSegment(sketch, "E7.2.1.2", {"start": v(10.53, 8.08) * mm, "end": v(5.93, 8.08) * mm});
            skLineSegment(sketch, "E7.2.1.3", {"start": v(10.53, -8.52) * mm, "end": v(5.93, -8.52) * mm});
            skLineSegment(sketch, "E7.3.1.0", {"start": v(3.93, 8.08) * mm, "end": v(3.93, -8.52) * mm});
            skLineSegment(sketch, "E7.3.1.1", {"start": v(-0.67, 8.08) * mm, "end": v(-0.67, -8.52) * mm});
            skLineSegment(sketch, "E7.3.1.2", {"start": v(3.93, 8.08) * mm, "end": v(-0.67, 8.08) * mm});
            skLineSegment(sketch, "E7.3.1.3", {"start": v(3.93, -8.52) * mm, "end": v(-0.67, -8.52) * mm});
            skLineSegment(sketch, "E7.4.0.0", {"start": v(-2.67, 26.68) * mm, "end": v(-2.67, 10.08) * mm});
            skLineSegment(sketch, "E7.4.0.1", {"start": v(-7.27, 26.68) * mm, "end": v(-7.27, 10.08) * mm});
            skLineSegment(sketch, "E7.4.0.2", {"start": v(-2.67, 26.68) * mm, "end": v(-7.27, 26.68) * mm});
            skLineSegment(sketch, "E7.4.0.3", {"start": v(-2.67, 10.08) * mm, "end": v(-7.27, 10.08) * mm});
            skLineSegment(sketch, "E7.4.1.0", {"start": v(-2.67, 8.08) * mm, "end": v(-2.67, -8.52) * mm});
            skLineSegment(sketch, "E7.4.1.1", {"start": v(-7.27, 8.08) * mm, "end": v(-7.27, -8.52) * mm});
            skLineSegment(sketch, "E7.4.1.2", {"start": v(-2.67, 8.08) * mm, "end": v(-7.27, 8.08) * mm});
            skLineSegment(sketch, "E7.4.1.3", {"start": v(-2.67, -8.52) * mm, "end": v(-7.27, -8.52) * mm});
            skLineSegment(sketch, "E7.5.0.0", {"start": v(-9.27, 26.68) * mm, "end": v(-9.27, 10.08) * mm});
            skLineSegment(sketch, "E7.5.0.1", {"start": v(-13.87, 26.68) * mm, "end": v(-13.87, 10.08) * mm});
            skLineSegment(sketch, "E7.5.0.2", {"start": v(-9.27, 26.68) * mm, "end": v(-13.87, 26.68) * mm});
            skLineSegment(sketch, "E7.5.0.3", {"start": v(-9.27, 10.08) * mm, "end": v(-13.87, 10.08) * mm});
            skLineSegment(sketch, "E7.5.1.0", {"start": v(-9.27, 8.08) * mm, "end": v(-9.27, -8.52) * mm});
            skLineSegment(sketch, "E7.5.1.1", {"start": v(-13.87, 8.08) * mm, "end": v(-13.87, -8.52) * mm});
            skLineSegment(sketch, "E7.5.1.2", {"start": v(-9.27, 8.08) * mm, "end": v(-13.87, 8.08) * mm});
            skLineSegment(sketch, "E7.5.1.3", {"start": v(-9.27, -8.52) * mm, "end": v(-13.87, -8.52) * mm});
            skLineSegment(sketch, "E7.6.0.0", {"start": v(-15.87, 26.68) * mm, "end": v(-15.87, 10.08) * mm});
            skLineSegment(sketch, "E7.6.0.1", {"start": v(-20.47, 26.68) * mm, "end": v(-20.47, 10.08) * mm});
            skLineSegment(sketch, "E7.6.0.2", {"start": v(-15.87, 26.68) * mm, "end": v(-20.47, 26.68) * mm});
            skLineSegment(sketch, "E7.6.0.3", {"start": v(-15.87, 10.08) * mm, "end": v(-20.47, 10.08) * mm});
            skLineSegment(sketch, "E7.6.1.0", {"start": v(-15.87, 8.08) * mm, "end": v(-15.87, -8.52) * mm});
            skLineSegment(sketch, "E7.6.1.1", {"start": v(-20.47, 8.08) * mm, "end": v(-20.47, -8.52) * mm});
            skLineSegment(sketch, "E7.6.1.2", {"start": v(-15.87, 8.08) * mm, "end": v(-20.47, 8.08) * mm});
            skLineSegment(sketch, "E7.6.1.3", {"start": v(-15.87, -8.52) * mm, "end": v(-20.47, -8.52) * mm});
            skSolve(sketch);
        }
        {
            var Q0;
            Q0 = qSketchRegion(id + "F4", true);
            extrude(context, id + "F5", {"entities" : qUnion([Q0]), "operationType" : NewBodyOperationType.REMOVE, "oppositeDirection" : true, "depth" : 1 * mm, "offsetDistance" : 25.4 * mm});
        }
    });
